# Revit family: Duct_Door-Acudor-Surface_Mount-HD-5070-F_Series
name_source: partatom
category: Specialty Equipment
revit_build: Autodesk Revit 2014 (Build: 20130308_1515(x64)
units: mm (PartAtom-declared; Revit-internal decimal feet)

## types (8) — shared parameters
Assembly Code = C1020700
Default Elevation = 0"
Description = Duct Door for Ductboard/Fiberglass
Finish = Galvanized Steel-Acudor-24 Gauge-Satin
Installation Type = Surface Mount
Length = 3/4"
Manufacturer = Acudor
Material = Galvanized Steel-Acudor-24 Gauge-Satin
Product Documentation Link = https://acudor.com
Product Page URL = https://acudor.com
URL = http://acudor.com

## per-type parameters (varying)
| type | Height | Width |
| HD-5070-F 6x6 | 6" | 6" |
| HD-5070-F 8x8 | 8" | 8" |
| HD-5070-F 10x10 | 10" | 10" |
| HD-5070-F 12x12 | 12" | 12" |
| HD-5070-F 14x14 | 14" | 14" |
| HD-5070-F 16x16 | 16" | 16" |
| HD-5070-F 18x18 | 18" | 18" |
| HD-5070-F 24x24 | 24" | 24" |

note: column(s) folded — value = type name in every type: Model

## geometry (parser evidence)
native form markers: Sweep x5
no freeform markers — native parametric forms only
